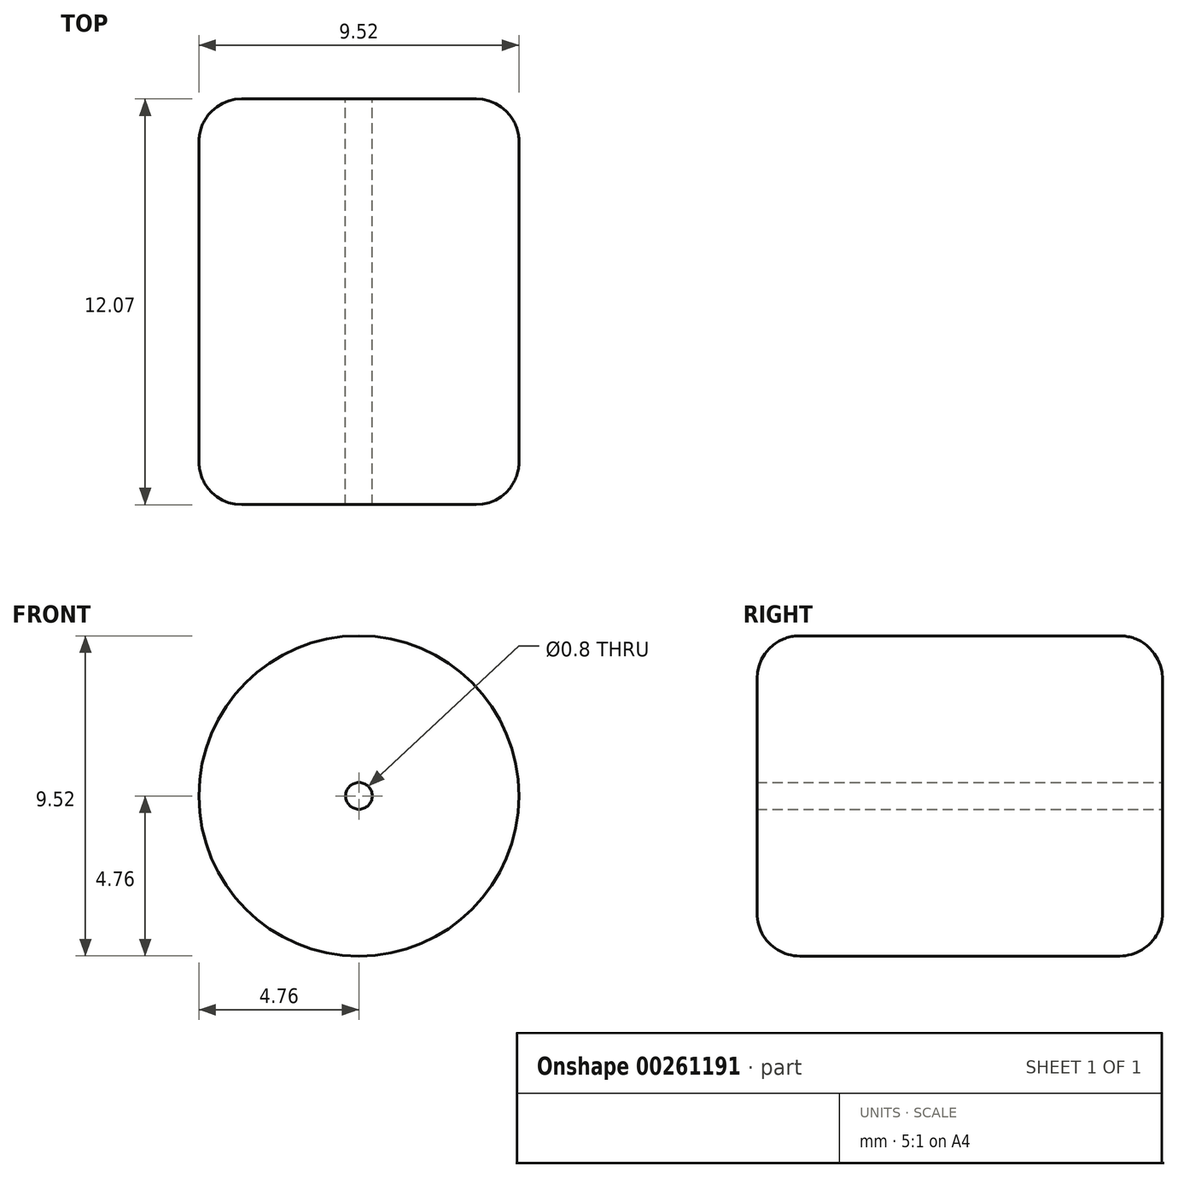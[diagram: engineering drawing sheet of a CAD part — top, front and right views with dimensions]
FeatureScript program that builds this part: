
annotation { "Feature Type Name" : "Feature", "Feature Type Description" : "" }
export const myFeature = defineFeature(function(context is Context, id is Id, definition is map)
    precondition{}
    {
        {
            var Q0;
            Q0=qCreatedBy(makeId("Front.planeOp"),FACE);
            var sketch = newSketch(context, id + "F0", { "sketchPlane" : qUnion([Q0])});
            skCircle(sketch, "E0", {"center": v(0, 0) * mm, "radius": 4.76 * mm});
            skSolve(sketch);
        }
        {
            var Q0;
            Q0=makeQuery(id+"F0.imprint","IMPRINT",FACE,{"disambiguationData":[TD([[makeQuery(id+"F0.imprint","IMPRINT",EDGE,{"derivedFrom":sQuery(id+"F0.wireOp",EDGE,"E0")}),1.0]])]});
            extrude(context, id + "F1", {"entities" : qUnion([Q0]), "depth" : 12.06 * mm});
        }
        {
            var Q0;
            Q0=makeQuery(id+"F1.opExtrude","CAP_EDGE",EDGE,{"disambiguationData":[OSD([sQuery(id+"F0.wireOp",EDGE,"E0")])],"isStart":false});
            var Q1;
            Q1=makeQuery(id+"F1.opExtrude","CAP_EDGE",EDGE,{"disambiguationData":[OSD([sQuery(id+"F0.wireOp",EDGE,"E0")])],"isStart":true});
            fillet(context, id + "F2", {"entities" : qUnion([Q0, Q1]), "radius" : 1.27 * mm, "tangentPropagation" : true, "allowEdgeOverflow" : false});
        }
        {
            var Q0;
            Q0=makeQuery(id+"F1.opExtrude","CAP_FACE",FACE,{"disambiguationData":[OSD([sQuery(id+"F0.wireOp",EDGE,"E0")])],"isStart":true});
            var sketch = newSketch(context, id + "F3", { "sketchPlane" : qUnion([Q0])});
            skPoint(sketch, "E1", {"position": v(0, 0) * mm});
            skSolve(sketch);
        }
        {
            var Q0;
            Q0=sQuery(id+"F3.wireOp",VERTEX,"E1");
            var Q1;
            Q1=makeQuery(id+"F1.opExtrude","SWEPT_BODY",BODY,{"disambiguationData":[OSD([sQuery(id+"F0.wireOp",EDGE,"E0")])]});
            hole(context, id + "F4", {"style" : HoleStyle.SIMPLE, "endStyle" : HoleEndStyle.THROUGH, "holeDiameter" : 0.8 * mm, "tappedDepth" : 25.4 * mm, "tapClearance" : 3, "startFromSketch" : true, "locations" : qUnion([Q0]), "scope" : qUnion([Q1])});
        }
    });
